# Revit family: HL_RU_Floor drain_HL300R-A-160411
name_source: partatom
category: Instalační zařizovací předměty
units: mm (PartAtom-declared; Revit-internal decimal feet)

## family parameters
Bod výpočtu místnosti = Ano
Kóta kulaté spojky = Použít průměr
Nadpis OmniClass = Deck Waste Water Drains
Ořezat dutým tvarem při načtení = Ne
Sdílené = Ano
Typ dílu = Normální
Vždy vertikální = Ano
Založené na pracovní rovině = Ne
Číslo OmniClass = 23.70.50.21.24.14

## types (1)
- 134_HL37N.1
    EAN = 9003076000340
    Indexovaná poznámka = HL300R
    Komentáře k typům = HL300R Трап для внутренних помещений DN50 горизонтальный с отверстием DN40/50, круглая насадка d 133мм/112мм
    Model = HL300R
    Popis = Трапы для внутренних помещений
    Přípoj CW = Ne
    Přípoj HW = Ne
    Přípoj odpadních dílů = Ano
    Přípoj ventilace = Ne
    URL = http://www.hutterer-lechner.com
    Výchozí výška = 0 mm  [stored 0 ft]
    Výrobce = HL Hutterer & Lechner GmbH
    ВЕС = 0,72 [kg]
    ВЫСОТА МОНТАЖА = 143 mm
    МАКСИМАЛЬНАЯ НАГРУЗКА КЛАССА = K3 - 300 kg
    МАТЕРИАЛ = PE
    НАСАДКА = d 112mm / V2A
    НОМИНАЛЬНЫЙ ДИАМЕТР = 50 mm
    ПРИЁМНОЕ ОТВЕРСТИЕ = DN40/50
    ПРОИЗВОДИТЕЛЬНОСТЬ = 0,5 l/sec
    ПРОПУСКНАЯ СПОСОБНОСТЬ = 0.0 L/s
    РАЗМЕР = DN50
    РЕШЁТКА = 20-75mm / d 133mm / PP-V2A

note: [stored X ft] marks values corroborated as IEEE doubles in the binary element streams (Revit-internal decimal feet)

## geometry (parser evidence)
native form markers: Sweep x36
no freeform markers — native parametric forms only
